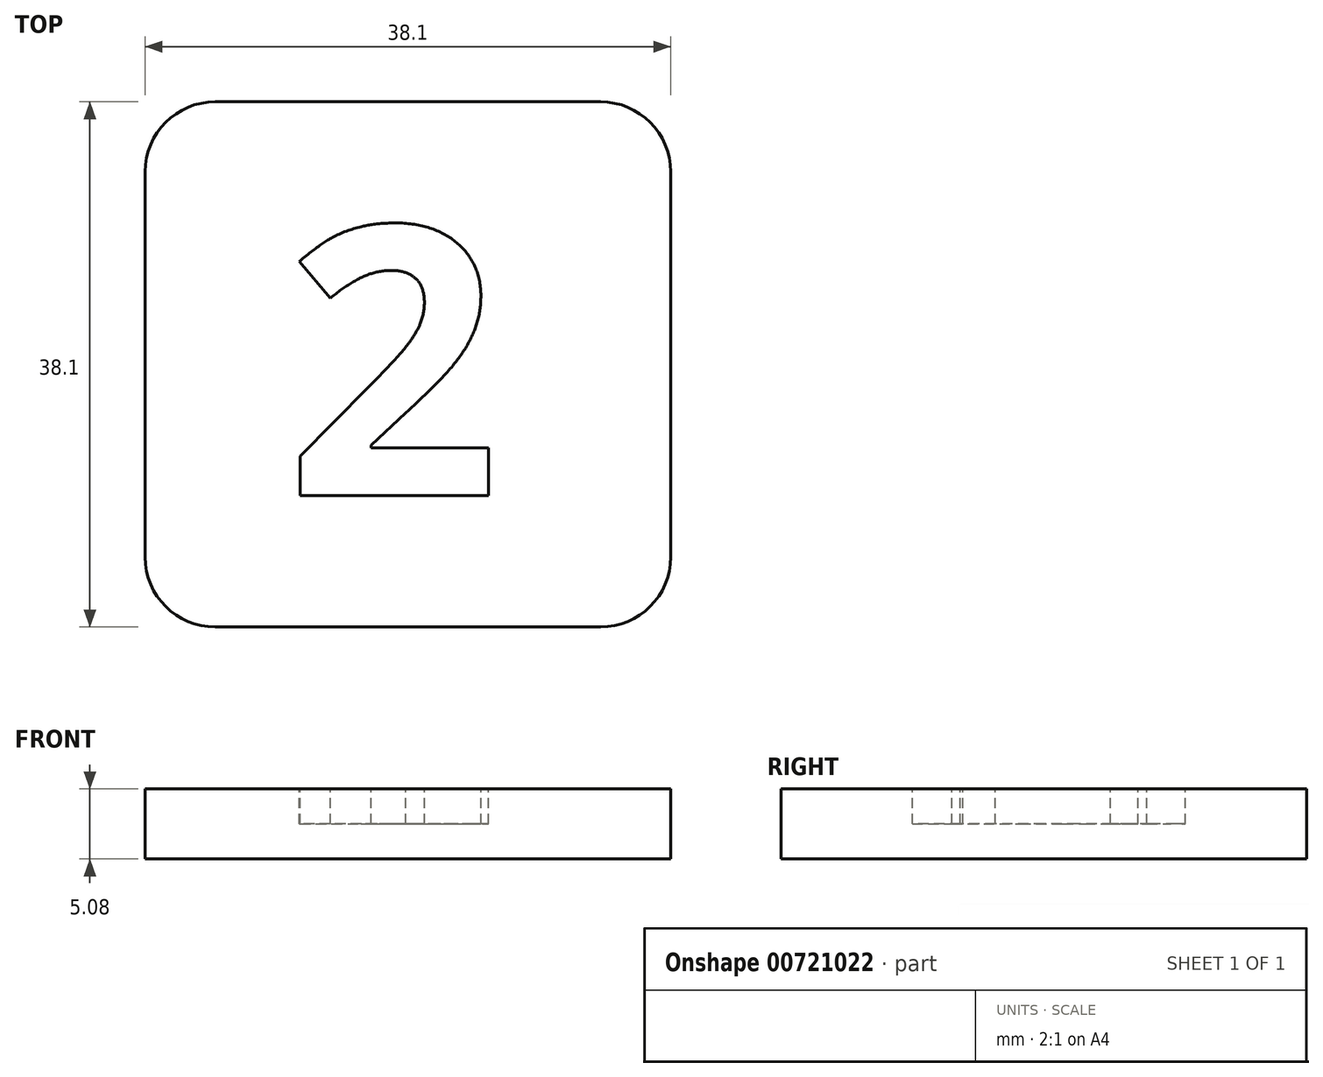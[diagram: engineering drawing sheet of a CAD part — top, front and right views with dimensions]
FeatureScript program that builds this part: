
annotation { "Feature Type Name" : "Feature", "Feature Type Description" : "" }
export const myFeature = defineFeature(function(context is Context, id is Id, definition is map)
    precondition{}
    {
        {
            var Q0;
            Q0=qCreatedBy(makeId("Top.planeOp"),FACE);
            var sketch = newSketch(context, id + "F0", { "sketchPlane" : qUnion([Q0])});
            skLineSegment(sketch, "E0.bottom", {"start": v(-19.05, 19.05) * mm, "end": v(19.05, 19.05) * mm});
            skLineSegment(sketch, "E0.top", {"start": v(-19.05, -19.05) * mm, "end": v(19.05, -19.05) * mm});
            skLineSegment(sketch, "E0.left", {"start": v(-19.05, 19.05) * mm, "end": v(-19.05, -19.05) * mm});
            skLineSegment(sketch, "E0.right", {"start": v(19.05, 19.05) * mm, "end": v(19.05, -19.05) * mm});
            skPoint(sketch, "E0.middle", {"position": v(0, 0) * mm});
            skSolve(sketch);
        }
        {
            var Q0;
            Q0=qSketchRegion(id+"F0",true);
            extrude(context, id + "F1", {"entities" : qUnion([Q0]), "depth" : 5.08 * mm, "offsetDistance" : 25.4 * mm});
        }
        {
            var Q0;
            Q0=makeQuery(id+"F1.opExtrude","CAP_FACE",FACE,{"disambiguationData":[OSD([sQuery(id+"F0.wireOp",EDGE,"E0.bottom"),sQuery(id+"F0.wireOp",EDGE,"E0.top"),sQuery(id+"F0.wireOp",EDGE,"E0.left"),sQuery(id+"F0.wireOp",EDGE,"E0.right")])],"isStart":false});
            var sketch = newSketch(context, id + "F2", { "sketchPlane" : qUnion([Q0])});
            skText(sketch, "E1", { "text": "2\n", "fontName": "OpenSans-Bold.ttf"});
            const initialGuessF2  = {"E1": [-0.0089, -0.00953, 1, 0, 0.01968]};
            skSetInitialGuess(sketch, initialGuessF2);
            skSolve(sketch);
        }
        {
            var Q0;
            Q0=qSketchRegion(id+"F2",true);
            extrude(context, id + "F3", {"entities" : qUnion([Q0]), "operationType" : NewBodyOperationType.REMOVE, "oppositeDirection" : true, "depth" : 2.54 * mm, "offsetDistance" : 25.4 * mm});
        }
        {
            var Q0;
            Q0=makeQuery(id+"F1.opExtrude","SWEPT_EDGE",EDGE,{"disambiguationData":[OSD([sQuery(id+"F0.wireOp",EDGE,"E0.top"),sQuery(id+"F0.wireOp",EDGE,"E0.left")])]});
            var Q1;
            Q1=makeQuery(id+"F1.opExtrude","SWEPT_EDGE",EDGE,{"disambiguationData":[OSD([sQuery(id+"F0.wireOp",EDGE,"E0.top"),sQuery(id+"F0.wireOp",EDGE,"E0.right")])]});
            var Q2;
            Q2=makeQuery(id+"F1.opExtrude","SWEPT_EDGE",EDGE,{"disambiguationData":[OSD([sQuery(id+"F0.wireOp",EDGE,"E0.bottom"),sQuery(id+"F0.wireOp",EDGE,"E0.right")])]});
            var Q3;
            Q3=makeQuery(id+"F1.opExtrude","SWEPT_EDGE",EDGE,{"disambiguationData":[OSD([sQuery(id+"F0.wireOp",EDGE,"E0.bottom"),sQuery(id+"F0.wireOp",EDGE,"E0.left")])]});
            fillet(context, id + "F4", {"entities" : qUnion([Q0, Q1, Q2, Q3]), "radius" : 5.08 * mm, "tangentPropagation" : true, "allowEdgeOverflow" : false});
        }
    });
